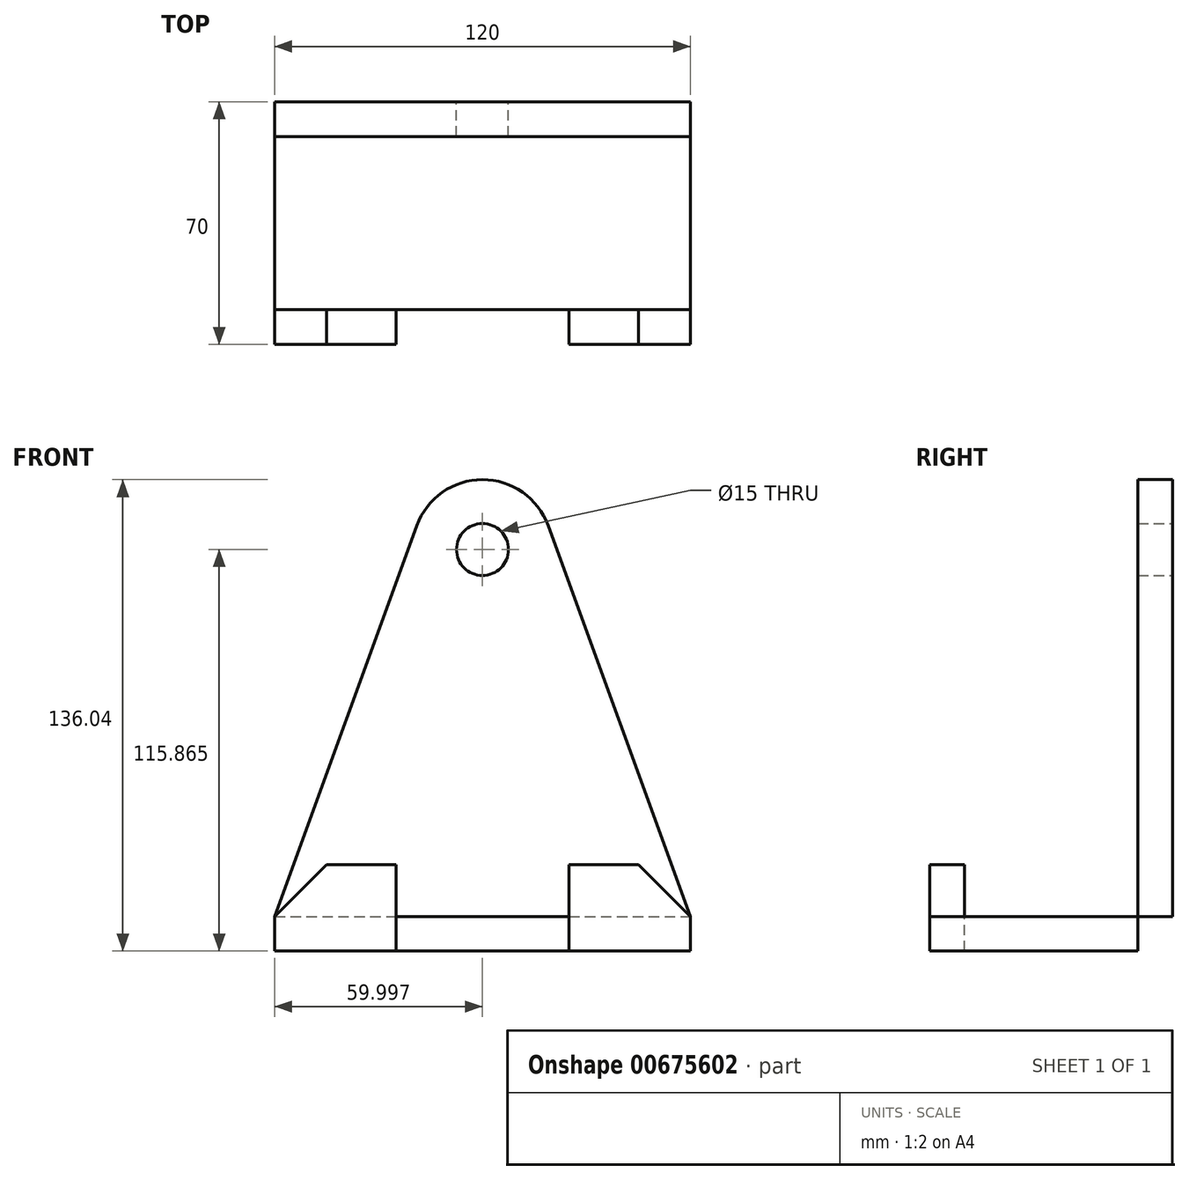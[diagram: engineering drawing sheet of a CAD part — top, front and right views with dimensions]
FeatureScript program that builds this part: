
annotation { "Feature Type Name" : "Feature", "Feature Type Description" : "" }
export const myFeature = defineFeature(function(context is Context, id is Id, definition is map)
    precondition{}
    {
        {
            var Q0;
            Q0=qCreatedBy(makeId("Front.planeOp"),FACE);
            var sketch = newSketch(context, id + "F0", { "sketchPlane" : qUnion([Q0])});
            skLineSegment(sketch, "E0", {"start": v(-61.13, -38.5) * mm, "end": v(58.87, -38.5) * mm});
            skLineSegment(sketch, "E1", {"start": v(58.87, -38.5) * mm, "end": v(17.82, 74.26) * mm});
            skLineSegment(sketch, "E2", {"start": v(-61.13, -38.5) * mm, "end": v(-20.1, 74.26) * mm});
            skArc(sketch, "E3", {"start": v(17.82, 74.26) * mm, "mid": v(-1.13, 87.53) * mm, "end": v(-20.1, 74.26) * mm});
            skLineSegment(sketch, "E4.top", {"start": v(-61.13, -48.5) * mm, "end": v(58.87, -48.5) * mm});
            skLineSegment(sketch, "E4.left", {"start": v(-61.13, -38.5) * mm, "end": v(-61.13, -48.5) * mm});
            skLineSegment(sketch, "E4.right", {"start": v(58.87, -38.5) * mm, "end": v(58.87, -48.5) * mm});
            skCircle(sketch, "E5", {"center": v(-1.13, 67.36) * mm, "radius": 7.5 * mm});
            skSolve(sketch);
        }
        {
            var Q0;
            Q0=makeQuery(id+"F0.imprint","IMPRINT",FACE,{"disambiguationData":[TD([[makeQuery(id+"F0.imprint","IMPRINT",EDGE,{"derivedFrom":sQuery(id+"F0.wireOp",EDGE,"E1")}),1.0]])]});
            var Q1;
            Q1=makeQuery(id+"F0.imprint","IMPRINT",FACE,{"disambiguationData":[TD([[makeQuery(id+"F0.imprint","IMPRINT",EDGE,{"derivedFrom":sQuery(id+"F0.wireOp",EDGE,"E0")}),-1.0]])]});
            extrude(context, id + "F1", {"entities" : qUnion([Q0, Q1]), "depth" : 10 * mm, "offsetDistance" : 25 * mm});
        }
        {
            var Q0;
            Q0=makeQuery(id+"F1.opExtrude","CAP_FACE",FACE,{"disambiguationData":[OSD([sQuery(id+"F0.wireOp",EDGE,"E1"),sQuery(id+"F0.wireOp",EDGE,"E2"),sQuery(id+"F0.wireOp",EDGE,"E3"),sQuery(id+"F0.wireOp",EDGE,"E4.top"),sQuery(id+"F0.wireOp",EDGE,"E4.left"),sQuery(id+"F0.wireOp",EDGE,"E4.right"),sQuery(id+"F0.wireOp",EDGE,"E5")])],"isStart":false});
            var sketch = newSketch(context, id + "F2", { "sketchPlane" : qUnion([Q0])});
            skLineSegment(sketch, "E6.bottom", {"start": v(-61.13, -48.5) * mm, "end": v(58.87, -48.5) * mm});
            skLineSegment(sketch, "E6.top", {"start": v(-61.13, -38.5) * mm, "end": v(58.87, -38.5) * mm});
            skLineSegment(sketch, "E6.left", {"start": v(-61.13, -48.5) * mm, "end": v(-61.13, -38.5) * mm});
            skLineSegment(sketch, "E6.right", {"start": v(58.87, -48.5) * mm, "end": v(58.87, -38.5) * mm});
            skSolve(sketch);
        }
        {
            var Q0;
            Q0 = qSketchRegion(id + "F2", true);
            extrude(context, id + "F3", {"entities" : qUnion([Q0]), "operationType" : NewBodyOperationType.ADD, "depth" : 50 * mm, "offsetDistance" : 25 * mm});
        }
        {
            var Q0;
            Q0=makeQuery(id+"F3.opExtrude","CAP_FACE",FACE,{"disambiguationData":[OSD([sQuery(id+"F2.wireOp",EDGE,"E6.bottom"),sQuery(id+"F2.wireOp",EDGE,"E6.top"),sQuery(id+"F2.wireOp",EDGE,"E6.left"),sQuery(id+"F2.wireOp",EDGE,"E6.right")])],"isStart":false});
            var sketch = newSketch(context, id + "F4", { "sketchPlane" : qUnion([Q0])});
            skLineSegment(sketch, "E7.bottom", {"start": v(-61.13, -48.5) * mm, "end": v(-26.13, -48.5) * mm});
            skLineSegment(sketch, "E7.top", {"start": v(-46.13, -23.5) * mm, "end": v(-26.13, -23.5) * mm});
            skLineSegment(sketch, "E7.left", {"start": v(-61.13, -48.5) * mm, "end": v(-61.13, -38.5) * mm});
            skLineSegment(sketch, "E7.right", {"start": v(-26.13, -48.5) * mm, "end": v(-26.13, -23.5) * mm});
            skLineSegment(sketch, "E8.bottom", {"start": v(58.87, -48.5) * mm, "end": v(23.87, -48.5) * mm});
            skLineSegment(sketch, "E8.top", {"start": v(43.87, -23.5) * mm, "end": v(23.87, -23.5) * mm});
            skLineSegment(sketch, "E8.left", {"start": v(58.87, -48.5) * mm, "end": v(58.87, -38.5) * mm});
            skLineSegment(sketch, "E8.right", {"start": v(23.87, -48.5) * mm, "end": v(23.87, -23.5) * mm});
            skLineSegment(sketch, "E9", {"start": v(-46.13, -23.5) * mm, "end": v(-61.13, -38.5) * mm});
            skLineSegment(sketch, "E10", {"start": v(43.87, -23.5) * mm, "end": v(58.87, -38.5) * mm});
            skPoint(sketch, "E11.orphan", {"position": v(-61.13, -23.5) * mm});
            skPoint(sketch, "E12.orphan", {"position": v(58.87, -23.5) * mm});
            skSolve(sketch);
        }
        {
            var Q0;
            {var subQ0=sQuery(id+"F4.wireOp",EDGE,"E8.top");Q0=makeQuery(id+"F4.imprint","IMPRINT",FACE,{"disambiguationData":[TD([[makeQuery(id+"F4.imprint","IMPRINT",EDGE,{"derivedFrom":subQ0}),1.0]])]});}
            var Q1;
            {var subQ0=sQuery(id+"F4.wireOp",EDGE,"E7.bottom");Q1=makeQuery(id+"F4.imprint","IMPRINT",FACE,{"disambiguationData":[TD([[makeQuery(id+"F4.imprint","IMPRINT",EDGE,{"derivedFrom":subQ0}),1.0]])]});}
            var Q2;
            {var subQ0=sQuery(id+"F4.wireOp",EDGE,"E8.bottom");Q2=makeQuery(id+"F4.imprint","IMPRINT",FACE,{"disambiguationData":[TD([[makeQuery(id+"F4.imprint","IMPRINT",EDGE,{"derivedFrom":subQ0}),1.0]])]});}
            var Q3;
            {var subQ0=sQuery(id+"F4.wireOp",EDGE,"E7.top");Q3=makeQuery(id+"F4.imprint","IMPRINT",FACE,{"disambiguationData":[TD([[makeQuery(id+"F4.imprint","IMPRINT",EDGE,{"derivedFrom":subQ0}),-1.0]])]});}
            extrude(context, id + "F5", {"entities" : qUnion([Q0, Q1, Q2, Q3]), "operationType" : NewBodyOperationType.ADD, "depth" : 10 * mm, "offsetDistance" : 25 * mm});
        }
    });
